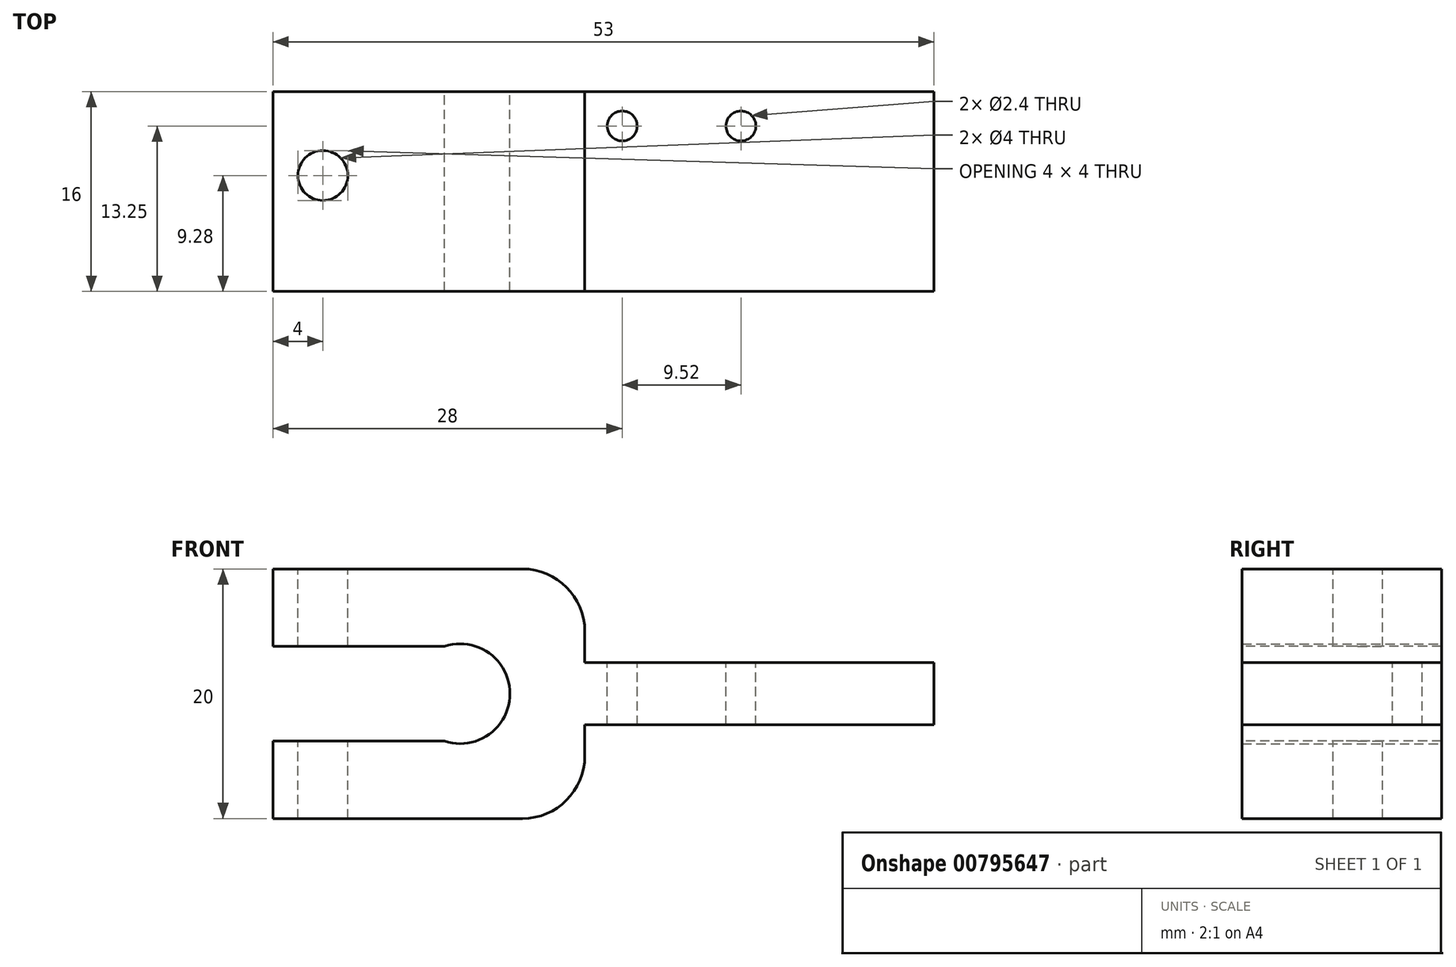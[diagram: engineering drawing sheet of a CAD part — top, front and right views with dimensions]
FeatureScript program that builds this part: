
annotation { "Feature Type Name" : "Feature", "Feature Type Description" : "" }
export const myFeature = defineFeature(function(context is Context, id is Id, definition is map)
    precondition{}
    {
        {
            var Q0;
            Q0=qCreatedBy(makeId("Top.planeOp"),FACE);
            var sketch = newSketch(context, id + "F0", { "sketchPlane" : qUnion([Q0])});
            skLineSegment(sketch, "E0.bottom", {"start": v(0, 0) * mm, "end": v(28, 0) * mm});
            skLineSegment(sketch, "E0.top", {"start": v(0, 16) * mm, "end": v(28, 16) * mm});
            skLineSegment(sketch, "E0.left", {"start": v(0, 0) * mm, "end": v(0, 16) * mm});
            skLineSegment(sketch, "E0.right", {"start": v(28, 0) * mm, "end": v(28, 16) * mm});
            skSolve(sketch);
        }
        {
            var Q0;
            Q0=makeQuery(id+"F0.imprint","IMPRINT",FACE,{"disambiguationData":[TD([[makeQuery(id+"F0.imprint","IMPRINT",EDGE,{"derivedFrom":sQuery(id+"F0.wireOp",EDGE,"E0.bottom")}),1.0]])]});
            extrude(context, id + "F1", {"entities" : qUnion([Q0]), "depth" : 5 * mm});
        }
        {
            var Q0;
            Q0=makeQuery(id+"F1.opExtrude","CAP_FACE",FACE,{"disambiguationData":[OSD([sQuery(id+"F0.wireOp",EDGE,"E0.bottom"),sQuery(id+"F0.wireOp",EDGE,"E0.top"),sQuery(id+"F0.wireOp",EDGE,"E0.left"),sQuery(id+"F0.wireOp",EDGE,"E0.right")])],"isStart":false});
            var sketch = newSketch(context, id + "F2", { "sketchPlane" : qUnion([Q0])});
            skCircle(sketch, "E1", {"center": v(12.52, 13.25) * mm, "radius": 1.2 * mm});
            skCircle(sketch, "E2", {"center": v(3, 13.25) * mm, "radius": 1.2 * mm});
            skSolve(sketch);
        }
        {
            var Q0;
            Q0=qSketchRegion(id+"F2",true);
            extrude(context, id + "F3", {"entities" : qUnion([Q0]), "operationType" : NewBodyOperationType.REMOVE, "endBound" : BoundingType.THROUGH_ALL, "oppositeDirection" : true, "depth" : 25 * mm});
        }
        {
            var Q0;
            Q0=makeQuery(id+"F1.opExtrude","SWEPT_FACE",FACE,{"disambiguationData":[OSD([sQuery(id+"F0.wireOp",EDGE,"E0.left")])]});
            var sketch = newSketch(context, id + "F4", { "sketchPlane" : qUnion([Q0])});
            skLineSegment(sketch, "E3.bottom", {"start": v(-16, 12.5) * mm, "end": v(0, 12.5) * mm});
            skLineSegment(sketch, "E3.top", {"start": v(-16, -7.5) * mm, "end": v(0, -7.5) * mm});
            skLineSegment(sketch, "E3.left", {"start": v(-16, 12.5) * mm, "end": v(-16, -7.5) * mm});
            skLineSegment(sketch, "E3.right", {"start": v(0, 12.5) * mm, "end": v(0, -7.5) * mm});
            skSolve(sketch);
        }
        {
            var Q0;
            Q0=qSketchRegion(id+"F4",true);
            extrude(context, id + "F5", {"entities" : qUnion([Q0]), "operationType" : NewBodyOperationType.ADD, "depth" : 25 * mm});
        }
        {
            var Q0;
            Q0=makeQuery(id+"F5.boolean.opBoolean","MERGE",FACE,{"derivedFrom":[makeQuery(id+"F1.opExtrude","SWEPT_FACE",FACE,{"disambiguationData":[OSD([sQuery(id+"F0.wireOp",EDGE,"E0.top")])]}),makeQuery(id+"F5.opExtrude","SWEPT_FACE",FACE,{"disambiguationData":[OSD([sQuery(id+"F4.wireOp",EDGE,"E3.left")])]})]});
            var sketch = newSketch(context, id + "F6", { "sketchPlane" : qUnion([Q0])});
            skCircle(sketch, "E4", {"center": v(10, 2.5) * mm, "radius": 4 * mm});
            skSolve(sketch);
        }
        {
            var Q0;
            Q0=qSketchRegion(id+"F6",true);
            extrude(context, id + "F7", {"entities" : qUnion([Q0]), "operationType" : NewBodyOperationType.REMOVE, "endBound" : BoundingType.THROUGH_ALL, "oppositeDirection" : true, "depth" : 25 * mm});
        }
        {
            var Q0;
            Q0=makeQuery(id+"F5.opExtrude","CAP_FACE",FACE,{"disambiguationData":[OSD([sQuery(id+"F4.wireOp",EDGE,"E3.bottom"),sQuery(id+"F4.wireOp",EDGE,"E3.top"),sQuery(id+"F4.wireOp",EDGE,"E3.left"),sQuery(id+"F4.wireOp",EDGE,"E3.right")])],"isStart":false});
            var sketch = newSketch(context, id + "F8", { "sketchPlane" : qUnion([Q0])});
            skLineSegment(sketch, "E5.bottom", {"start": v(-16, -1.3) * mm, "end": v(0, -1.3) * mm});
            skLineSegment(sketch, "E5.top", {"start": v(-16, 6.3) * mm, "end": v(0, 6.3) * mm});
            skLineSegment(sketch, "E5.left", {"start": v(-16, -1.3) * mm, "end": v(-16, 6.3) * mm});
            skLineSegment(sketch, "E5.right", {"start": v(0, -1.3) * mm, "end": v(0, 6.3) * mm});
            skSolve(sketch);
        }
        {
            var Q0;
            Q0=makeQuery(id+"F8.imprint","IMPRINT",FACE,{"disambiguationData":[TD([[makeQuery(id+"F8.imprint","IMPRINT",EDGE,{"derivedFrom":sQuery(id+"F8.wireOp",EDGE,"E5.bottom")}),1.0]])]});
            extrude(context, id + "F9", {"entities" : qUnion([Q0]), "operationType" : NewBodyOperationType.REMOVE, "oppositeDirection" : true, "depth" : 10 * mm});
        }
        {
            var Q0;
            Q0=makeQuery(id+"F5.opExtrude","SWEPT_FACE",FACE,{"disambiguationData":[OSD([sQuery(id+"F4.wireOp",EDGE,"E3.bottom")])]});
            var sketch = newSketch(context, id + "F10", { "sketchPlane" : qUnion([Q0])});
            skCircle(sketch, "E6", {"center": v(-21, 9.28) * mm, "radius": 2 * mm});
            skSolve(sketch);
        }
        {
            var Q0;
            Q0=qSketchRegion(id+"F10",true);
            extrude(context, id + "F11", {"entities" : qUnion([Q0]), "operationType" : NewBodyOperationType.REMOVE, "endBound" : BoundingType.THROUGH_ALL, "oppositeDirection" : true, "depth" : 25 * mm});
        }
        {
            var Q0;
            Q0=qSketchRegion(id+"F8",true);
            extrude(context, id + "F12", {"entities" : qUnion([Q0]), "operationType" : NewBodyOperationType.REMOVE, "oppositeDirection" : true, "depth" : 15 * mm});
        }
        {
            var Q0;
            Q0=makeQuery(id+"F5.opExtrude","CAP_EDGE",EDGE,{"disambiguationData":[OSD([sQuery(id+"F4.wireOp",EDGE,"E3.bottom")])],"isStart":true});
            fillet(context, id + "F13", {"entities" : qUnion([Q0]), "radius" : 5 * mm, "tangentPropagation" : true, "allowEdgeOverflow" : false});
        }
        {
            var Q0;
            Q0=makeQuery(id+"F5.opExtrude","CAP_EDGE",EDGE,{"disambiguationData":[OSD([sQuery(id+"F4.wireOp",EDGE,"E3.top")])],"isStart":true});
            fillet(context, id + "F14", {"entities" : qUnion([Q0]), "radius" : 5 * mm, "tangentPropagation" : true, "allowEdgeOverflow" : false});
        }
    });
